# Revit family: Accessories-Teknion-CEAUC_Undercabinet_Cubby-R2022
name_source: partatom
category: Furniture
units: mm (PartAtom-declared; Revit-internal decimal feet)

## family parameters
Always vertical = Yes
Cut with Voids When Loaded = No
OmniClass Number = 23.40.20.00
OmniClass Title = General Furniture and Specialties
Render Appearance Source = Family Geometry
Room Calculation Point = No
Shared = Yes
Work Plane-Based = No

## types (2) — shared parameters
Assembly Code = E2020200
Manufacturer = Teknion
Manufacturer Fax = 416.661.4586
Part Number = CEAUC
Product Documentation Link = https://www.teknion.com
Product Line = Accessories
Product Page URL = https://www.teknion.com
Series = Expansion Casework+
Sustainability Data = https://www.teknion.com
URL = www.teknion.com
Unit Weight URL = http://www.teknion.com
Warranty = http://www.teknion.com
zero-valued in all types: Default Elevation

## per-type parameters (varying)
| type | Depth | Description | Model |
| 15" Depth | 14.161 " | Undercabinet Cubby, 15"D, 9" Height | CEAUC15_09 |
| 12" Depth | 11.161 " | Undercabinet Cubby, 12"D, 9" Height | CEAUC11_09 |

## geometry (parser evidence)
native form markers: Sweep x3
no freeform markers — native parametric forms only
